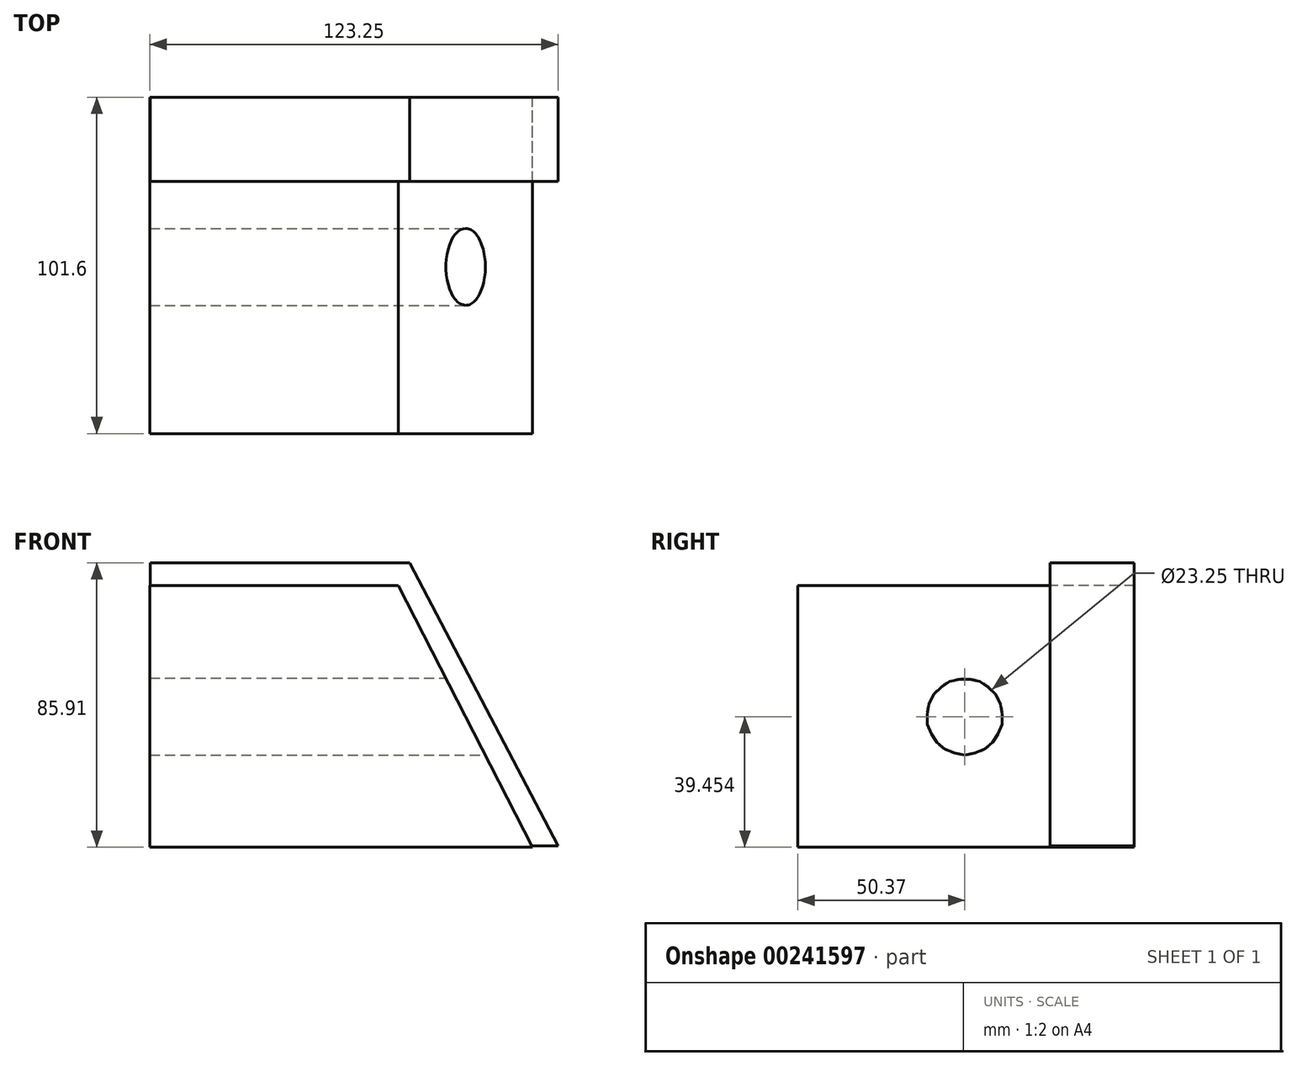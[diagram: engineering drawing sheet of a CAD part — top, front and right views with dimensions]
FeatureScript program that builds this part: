
annotation { "Feature Type Name" : "Feature", "Feature Type Description" : "" }
export const myFeature = defineFeature(function(context is Context, id is Id, definition is map)
    precondition{}
    {
        {
            var Q0;
            Q0=qCreatedBy(makeId("Front.planeOp"),FACE);
            var sketch = newSketch(context, id + "F0", { "sketchPlane" : qUnion([Q0])});
            skLineSegment(sketch, "E0.bottom", {"start": v(-35.67, 28.4) * mm, "end": v(39.36, 28.4) * mm});
            skLineSegment(sketch, "E0.top", {"start": v(-35.67, -50.7) * mm, "end": v(39.36, -50.7) * mm});
            skLineSegment(sketch, "E0.left", {"start": v(-35.67, 28.4) * mm, "end": v(-35.67, -50.7) * mm});
            skLineSegment(sketch, "E1", {"start": v(39.36, 28.4) * mm, "end": v(79.92, -50.7) * mm});
            skLineSegment(sketch, "E2", {"start": v(39.36, -50.7) * mm, "end": v(79.92, -50.7) * mm});
            skSolve(sketch);
        }
        {
            var Q0;
            Q0=makeQuery(id+"F0.imprint","IMPRINT",FACE,{"disambiguationData":[TD([[makeQuery(id+"F0.imprint","IMPRINT",EDGE,{"derivedFrom":sQuery(id+"F0.wireOp",EDGE,"E0.bottom")}),-1.0]])]});
            extrude(context, id + "F1", {"entities" : qUnion([Q0]), "depth" : 101.6 * mm});
        }
        {
            var Q0;
            Q0=qCreatedBy(makeId("Right.planeOp"),FACE);
            var sketch = newSketch(context, id + "F2", { "sketchPlane" : qUnion([Q0])});
            skCircle(sketch, "E3", {"center": v(-51.23, -11.25) * mm, "radius": 11.63 * mm});
            skSolve(sketch);
        }
        {
            var Q0;
            Q0 = qSketchRegion(id + "F2", true);
            extrude(context, id + "F3", {"entities" : qUnion([Q0]), "operationType" : NewBodyOperationType.REMOVE, "endBound" : BoundingType.SYMMETRIC, "oppositeDirection" : true, "depth" : 177.8 * mm, "hasSecondDirection" : true, "secondDirectionOppositeDirection" : false, "secondDirectionDepth" : 25.4 * mm});
        }
        {
            var Q0;
            Q0=qCreatedBy(makeId("Front.planeOp"),FACE);
            var sketch = newSketch(context, id + "F4", { "sketchPlane" : qUnion([Q0])});
            skLineSegment(sketch, "E4.bottom", {"start": v(-35.56, -50.33) * mm, "end": v(87.58, -50.33) * mm});
            skLineSegment(sketch, "E4.left", {"start": v(-35.56, -50.33) * mm, "end": v(-35.56, 35.21) * mm});
            skLineSegment(sketch, "E5", {"start": v(42.79, 35.21) * mm, "end": v(87.58, -50.33) * mm});
            skLineSegment(sketch, "E6", {"start": v(42.79, 35.21) * mm, "end": v(-35.56, 35.21) * mm});
            skSolve(sketch);
        }
        {
            var Q0;
            Q0 = qSketchRegion(id + "F4", true);
            extrude(context, id + "F5", {"entities" : qUnion([Q0]), "operationType" : NewBodyOperationType.ADD, "depth" : 25.4 * mm});
        }
    });
